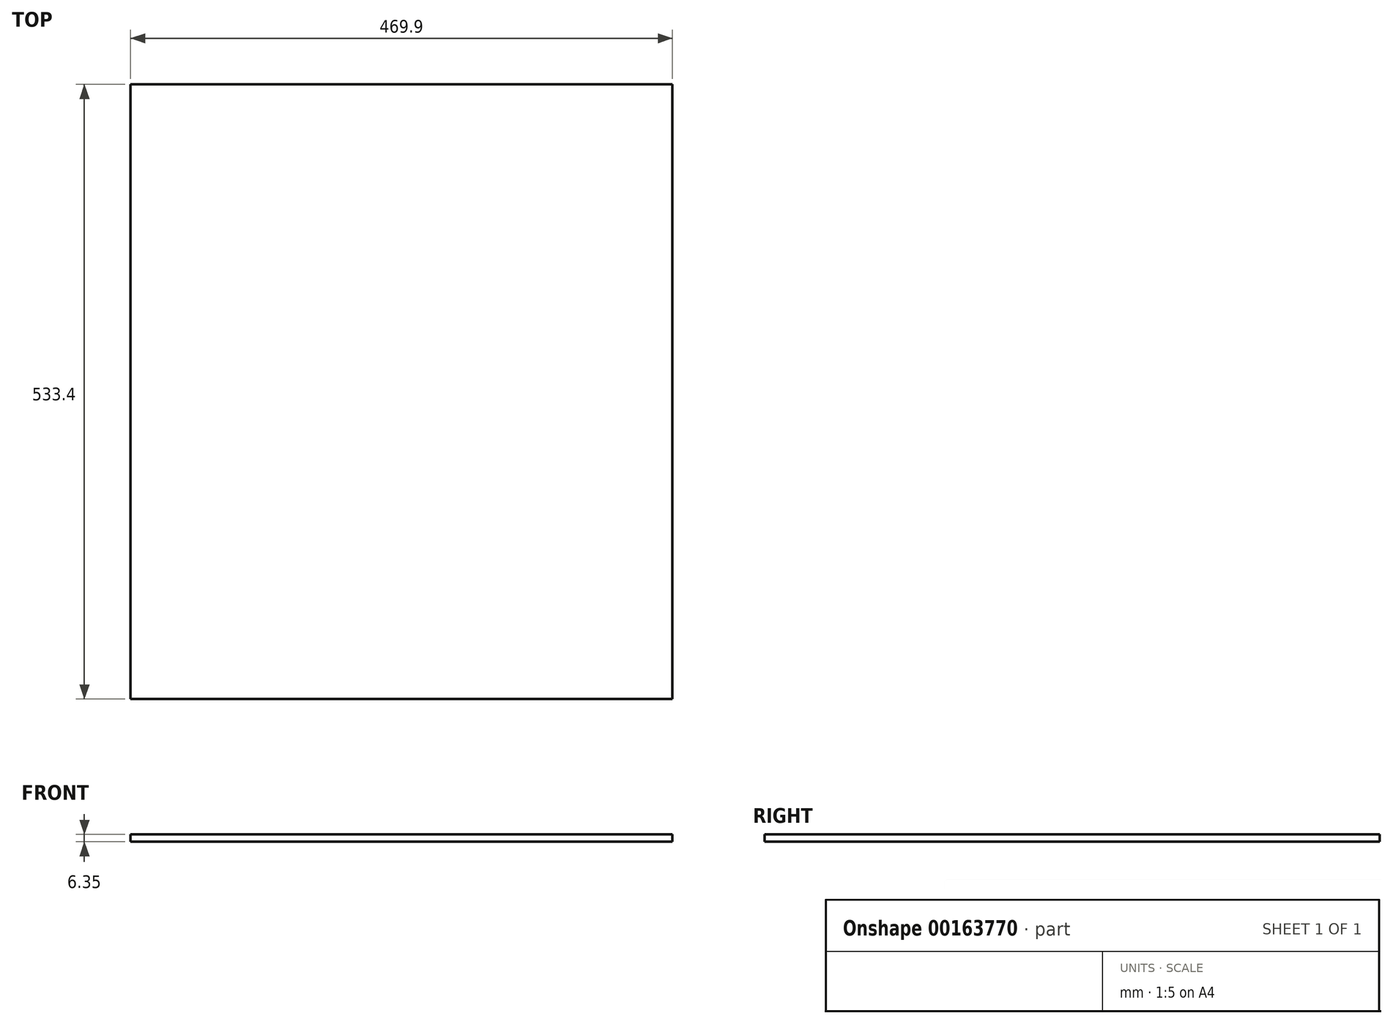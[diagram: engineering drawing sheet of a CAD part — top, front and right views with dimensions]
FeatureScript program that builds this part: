
annotation { "Feature Type Name" : "Feature", "Feature Type Description" : "" }
export const myFeature = defineFeature(function(context is Context, id is Id, definition is map)
    precondition{}
    {
        {
            var Q0;
            Q0=qCreatedBy(makeId("Top.planeOp"),FACE);
            var sketch = newSketch(context, id + "F0", { "sketchPlane" : qUnion([Q0])});
            skLineSegment(sketch, "E0.bottom", {"start": v(234.95, 266.7) * mm, "end": v(-234.95, 266.7) * mm});
            skLineSegment(sketch, "E0.top", {"start": v(234.95, -266.7) * mm, "end": v(-234.95, -266.7) * mm});
            skLineSegment(sketch, "E0.left", {"start": v(234.95, 266.7) * mm, "end": v(234.95, -266.7) * mm});
            skLineSegment(sketch, "E0.right", {"start": v(-234.95, 266.7) * mm, "end": v(-234.95, -266.7) * mm});
            skPoint(sketch, "E0.middle", {"position": v(0, 0) * mm});
            skSolve(sketch);
        }
        {
            var Q0;
            Q0 = qSketchRegion(id + "F0", true);
            extrude(context, id + "F1", {"entities" : qUnion([Q0]), "depth" : 6.35 * mm, "offsetDistance" : 25.4 * mm});
        }
    });
